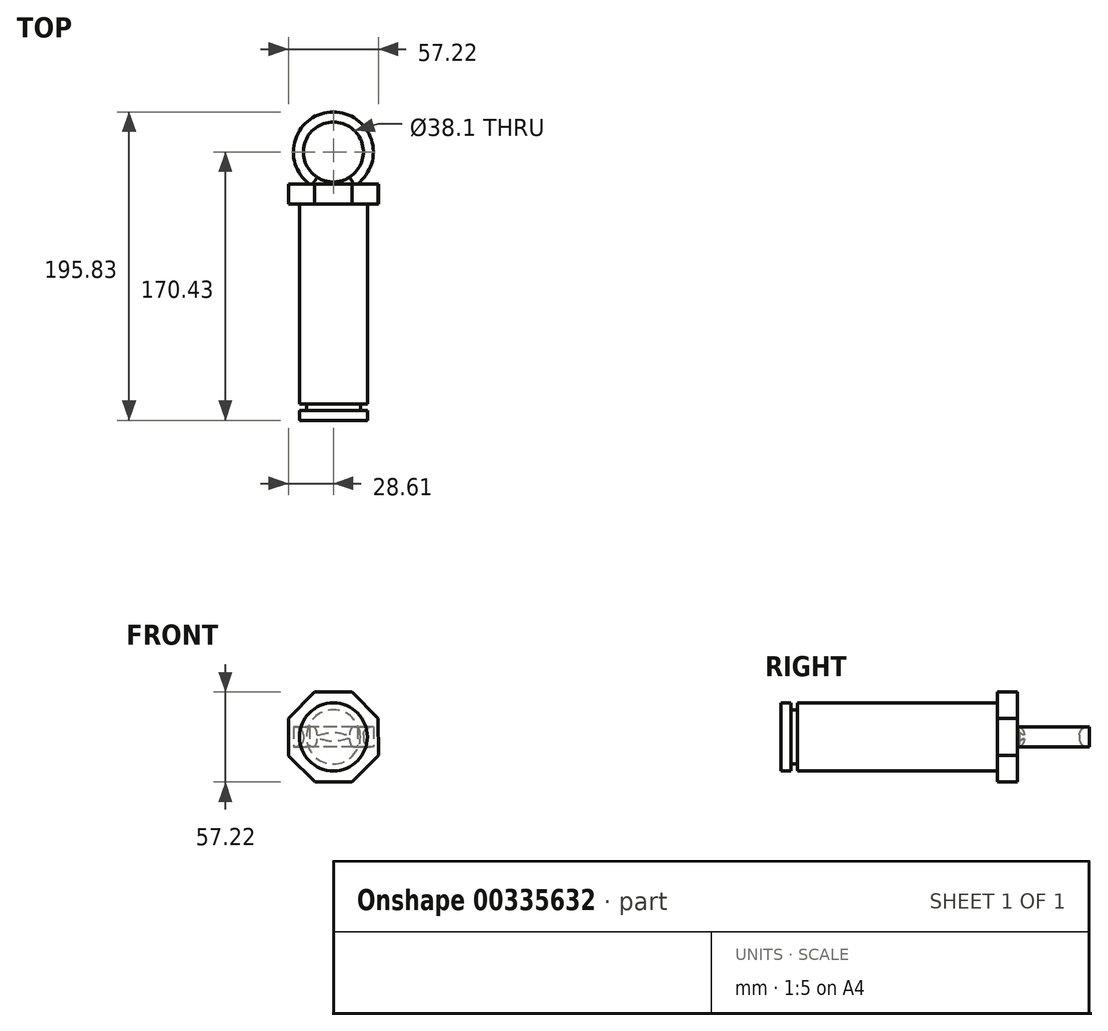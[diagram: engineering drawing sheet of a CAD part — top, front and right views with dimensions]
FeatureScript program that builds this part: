
annotation { "Feature Type Name" : "Feature", "Feature Type Description" : "" }
export const myFeature = defineFeature(function(context is Context, id is Id, definition is map)
    precondition{}
    {
        {
            var Q0;
            Q0=qCreatedBy(makeId("Front.planeOp"),FACE);
            var sketch = newSketch(context, id + "F0", { "sketchPlane" : qUnion([Q0])});
            skCircle(sketch, "E0.cCircle", {"center": v(0, 0) * mm, "radius": 28.58 * mm, "construction": true});
            skLineSegment(sketch, "E0.0", {"start": v(-28.6, 11.76) * mm, "end": v(-11.91, 28.54) * mm});
            skLineSegment(sketch, "E0.1", {"start": v(-11.91, 28.54) * mm, "end": v(11.76, 28.6) * mm});
            skLineSegment(sketch, "E0.2", {"start": v(11.76, 28.6) * mm, "end": v(28.54, 11.91) * mm});
            skLineSegment(sketch, "E0.3", {"start": v(28.54, 11.91) * mm, "end": v(28.6, -11.76) * mm});
            skLineSegment(sketch, "E0.4", {"start": v(28.6, -11.76) * mm, "end": v(11.91, -28.54) * mm});
            skLineSegment(sketch, "E0.5", {"start": v(11.91, -28.54) * mm, "end": v(-11.76, -28.6) * mm});
            skLineSegment(sketch, "E0.6", {"start": v(-11.76, -28.6) * mm, "end": v(-28.54, -11.91) * mm});
            skLineSegment(sketch, "E0.7", {"start": v(-28.54, -11.91) * mm, "end": v(-28.6, 11.76) * mm});
            skPoint(sketch, "E0.0.midPoint", {"position": v(-20.26, 20.15) * mm});
            skSolve(sketch);
        }
        {
            var Q0;
            Q0=makeQuery(id+"F0.imprint","IMPRINT",FACE,{"disambiguationData":[TD([[makeQuery(id+"F0.imprint","IMPRINT",EDGE,{"derivedFrom":sQuery(id+"F0.wireOp",EDGE,"E0.0")}),-1.0]])]});
            extrude(context, id + "F1", {"entities" : qUnion([Q0]), "depth" : 12.7 * mm});
        }
        {
            var Q0;
            Q0=makeQuery(id+"F1.opExtrude","CAP_FACE",FACE,{"disambiguationData":[OSD([sQuery(id+"F0.wireOp",EDGE,"E0.0"),sQuery(id+"F0.wireOp",EDGE,"E0.1"),sQuery(id+"F0.wireOp",EDGE,"E0.2"),sQuery(id+"F0.wireOp",EDGE,"E0.3"),sQuery(id+"F0.wireOp",EDGE,"E0.4"),sQuery(id+"F0.wireOp",EDGE,"E0.5"),sQuery(id+"F0.wireOp",EDGE,"E0.6"),sQuery(id+"F0.wireOp",EDGE,"E0.7")])],"isStart":false});
            var sketch = newSketch(context, id + "F2", { "sketchPlane" : qUnion([Q0])});
            skCircle(sketch, "E1", {"center": v(0, 0) * mm, "radius": 21.59 * mm});
            skSolve(sketch);
        }
        {
            var Q0;
            Q0 = qSketchRegion(id + "F2", true);
            extrude(context, id + "F3", {"entities" : qUnion([Q0]), "operationType" : NewBodyOperationType.ADD, "depth" : 127 * mm});
        }
        {
            var Q0;
            Q0=makeQuery(id+"F3.opExtrude","CAP_FACE",FACE,{"disambiguationData":[OSD([sQuery(id+"F2.wireOp",EDGE,"E1")])],"isStart":false});
            var sketch = newSketch(context, id + "F4", { "sketchPlane" : qUnion([Q0])});
            skCircle(sketch, "E2", {"center": v(0, 0) * mm, "radius": 17.17 * mm});
            skSolve(sketch);
        }
        {
            var Q0;
            Q0 = qSketchRegion(id + "F4", true);
            extrude(context, id + "F5", {"entities" : qUnion([Q0]), "operationType" : NewBodyOperationType.ADD, "depth" : 4.06 * mm});
        }
        {
            var Q0;
            Q0=makeQuery(id+"F5.opExtrude","CAP_FACE",FACE,{"disambiguationData":[OSD([sQuery(id+"F4.wireOp",EDGE,"E2")])],"isStart":false});
            var sketch = newSketch(context, id + "F6", { "sketchPlane" : qUnion([Q0])});
            skCircle(sketch, "E3", {"center": v(0, 0) * mm, "radius": 21.6 * mm});
            skSolve(sketch);
        }
        {
            var Q0;
            Q0 = qSketchRegion(id + "F6", true);
            extrude(context, id + "F7", {"entities" : qUnion([Q0]), "operationType" : NewBodyOperationType.ADD, "depth" : 6.35 * mm});
        }
        {
            var Q0;
            Q0=qCreatedBy(makeId("Top.planeOp"),FACE);
            var sketch = newSketch(context, id + "F8", { "sketchPlane" : qUnion([Q0])});
            skLineSegment(sketch, "E4", {"start": v(0, 0) * mm, "end": v(0, 20.32) * mm});
            skCircle(sketch, "E5", {"center": v(0, 20.32) * mm, "radius": 25.4 * mm});
            skCircle(sketch, "E6", {"center": v(0, 20.32) * mm, "radius": 19.05 * mm});
            skSolve(sketch);
        }
        {
            var Q0;
            Q0 = qSketchRegion(id + "F8", true);
            extrude(context, id + "F9", {"entities" : qUnion([Q0]), "operationType" : NewBodyOperationType.ADD, "depth" : 6.35 * mm, "hasSecondDirection" : true, "secondDirectionOppositeDirection" : true, "secondDirectionDepth" : 6.35 * mm});
        }
        {
            var Q0;
            Q0=makeQuery(id+"F9.opExtrude","CAP_EDGE",EDGE,{"disambiguationData":[OSD([sQuery(id+"F8.wireOp",EDGE,"E6")])],"isStart":false});
            var Q1;
            Q1=makeQuery(id+"F9.opExtrude","CAP_EDGE",EDGE,{"disambiguationData":[OSD([sQuery(id+"F8.wireOp",EDGE,"E6")])],"isStart":true});
            fillet(context, id + "F10", {"entities" : qUnion([Q0, Q1]), "radius" : 5.08 * mm, "tangentPropagation" : true, "allowEdgeOverflow" : false});
        }
    });
